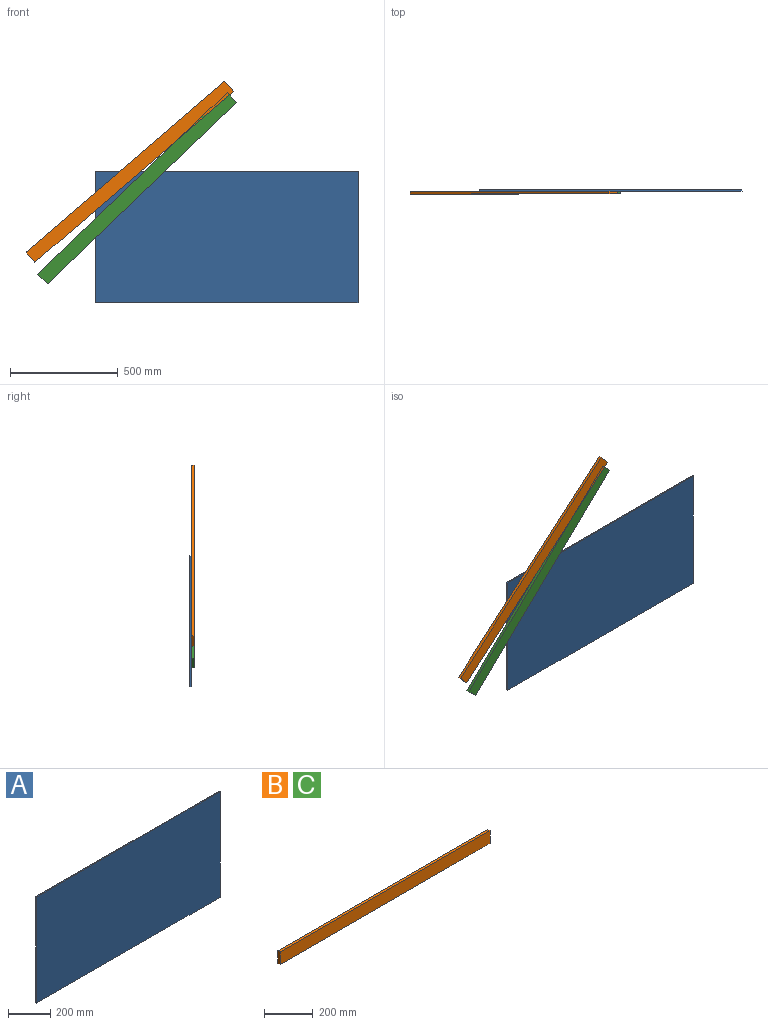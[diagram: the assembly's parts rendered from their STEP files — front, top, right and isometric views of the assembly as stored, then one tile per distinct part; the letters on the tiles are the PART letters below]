
ASSEMBLY  parts=3 mates=2
PART A: 6 faces, bbox 1219.9x6.4x610.3 mm
  f0: plane 610.27x6.35mm, normal (-1,0.05,0), area 3878.4mm2, adj f1,f3,f4,f5
  f1: plane 1219.87x6.35mm, normal (0,0.05,-1), area 7754.7mm2, adj f0,f2,f4,f5
  f2: plane 610.27x6.35mm, normal (1,0.05,0), area 3878.4mm2, adj f1,f3,f4,f5
  f3: plane 1219.87x6.35mm, normal (0,0.05,1), area 7754.7mm2, adj f0,f2,f4,f5
  f4: plane 1219.87x610.27mm, normal (0,-1,0), area 744442mm2, adj f0,f1,f2,f3
  f5: plane 1219.2x609.6mm, normal (0,1,0), area 743224.3mm2, adj f0,f1,f2,f3
PART B: 6 faces, bbox 1219.2x12.7x63.5 mm
  f0: plane 63.5x12.7mm, normal (1,0,0), area 806.5mm2, adj f1,f3,f4,f5
  f1: plane 1219.2x12.7mm, normal (0,0,1), area 15483.8mm2, adj f0,f2,f4,f5
  f2: plane 63.5x12.7mm, normal (-1,0,0), area 806.5mm2, adj f1,f3,f4,f5
  f3: plane 1219.2x12.7mm, normal (0,0,-1), area 15483.8mm2, adj f0,f2,f4,f5
  f4: plane 1219.2x63.5mm, normal (0,-1,0), area 77419.2mm2, adj f0,f1,f2,f3
  f5: plane 1219.2x63.5mm, normal (0,1,0), area 77419.2mm2, adj f0,f1,f2,f3
PART C: same geometry as B
PLACE A t=(-39.31,334.63,-36.78)mm
PLACE B rot(axis=(0,-1,0),40.7deg) t=(-29.31,328.28,-696.03)mm
PLACE C rot(axis=(0,-1,0),43.8deg) t=(52.33,328.28,-774.68)mm
MATE planar A.f4 <-> C.f5  axis (0,-1,0) through (471.76,328.28,-124.08)mm
MATE planar A.f4 <-> B.f5  axis (0,-1,0) through (471.76,328.28,-124.08)mm
